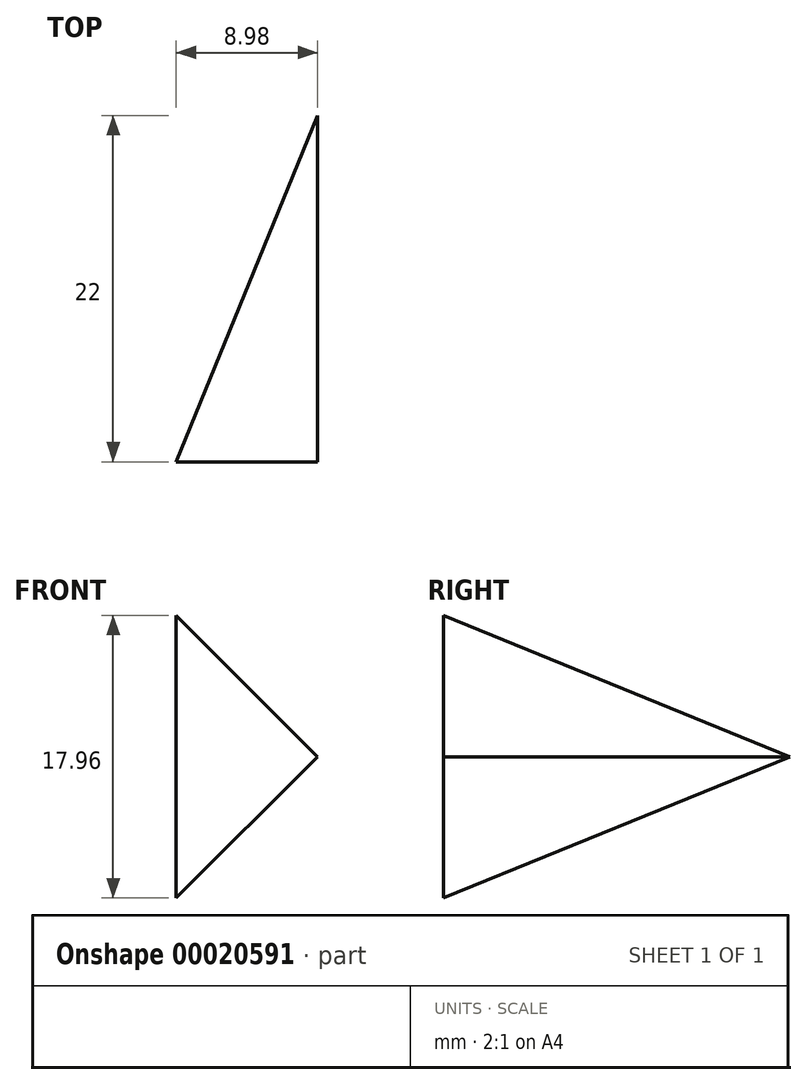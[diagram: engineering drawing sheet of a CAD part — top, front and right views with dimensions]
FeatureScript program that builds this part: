
annotation { "Feature Type Name" : "Feature", "Feature Type Description" : "" }
export const myFeature = defineFeature(function(context is Context, id is Id, definition is map)
    precondition{}
    {
        {
            var Q0;
            Q0=qCreatedBy(makeId("Top.planeOp"),FACE);
            var sketch = newSketch(context, id + "F0", { "sketchPlane" : qUnion([Q0])});
            skLineSegment(sketch, "E0", {"start": v(0, 0) * mm, "end": v(-12.7, 0) * mm});
            skLineSegment(sketch, "E1", {"start": v(-12.7, 0) * mm, "end": v(0, 22) * mm});
            skLineSegment(sketch, "E2", {"start": v(0, 0) * mm, "end": v(0, 22) * mm});
            skSolve(sketch);
        }
        {
            var Q0;
            Q0=qCreatedBy(makeId("Right.planeOp"),FACE);
            var sketch = newSketch(context, id + "F1", { "sketchPlane" : qUnion([Q0])});
            skLineSegment(sketch, "E3", {"start": v(0, 0) * mm, "end": v(0, -12.7) * mm});
            skLineSegment(sketch, "E4", {"start": v(0, 0) * mm, "end": v(0, 15.02) * mm});
            skSolve(sketch);
        }
        {
            var Q0;
            Q0=sQuery(id+"F1.wireOp",VERTEX,"E3.end");
            var Q1;
            Q1=makeQuery(id+"F0.imprint","IMPRINT",FACE,{"disambiguationData":[TD([[makeQuery(id+"F0.imprint","IMPRINT",EDGE,{"derivedFrom":sQuery(id+"F0.wireOp",EDGE,"E0")}),-1.0]])]});
            loft(context, id + "F2", {"sheetProfilesArray" : [{ "sheetProfileEntities" : qUnion([Q0]) }, { "sheetProfileEntities" : qUnion([Q1]) }]});
        }
        {
            var Q0;
            Q0=makeQuery(id+"F2.opLoft","SWEPT_BODY",BODY,{"disambiguationData":[OSD([makeQuery(id+"F0.imprint","IMPRINT",FACE,{"disambiguationData":[TD([[makeQuery(id+"F0.imprint","IMPRINT",EDGE,{"derivedFrom":sQuery(id+"F0.wireOp",EDGE,"E0")}),-1.0]])]}),sQuery(id+"F1.wireOp",VERTEX,"E3.end")])]});
            var Q1;
            Q1=sQuery(id+"F0.wireOp",EDGE,"E2");
            transform(context, id + "F3", {"entities" : qUnion([Q0]), "transformType" : TransformType.ROTATION, "transformAxis" : qUnion([Q1]), "angle" : 45 * degree, "makeCopy" : false});
        }
    });
